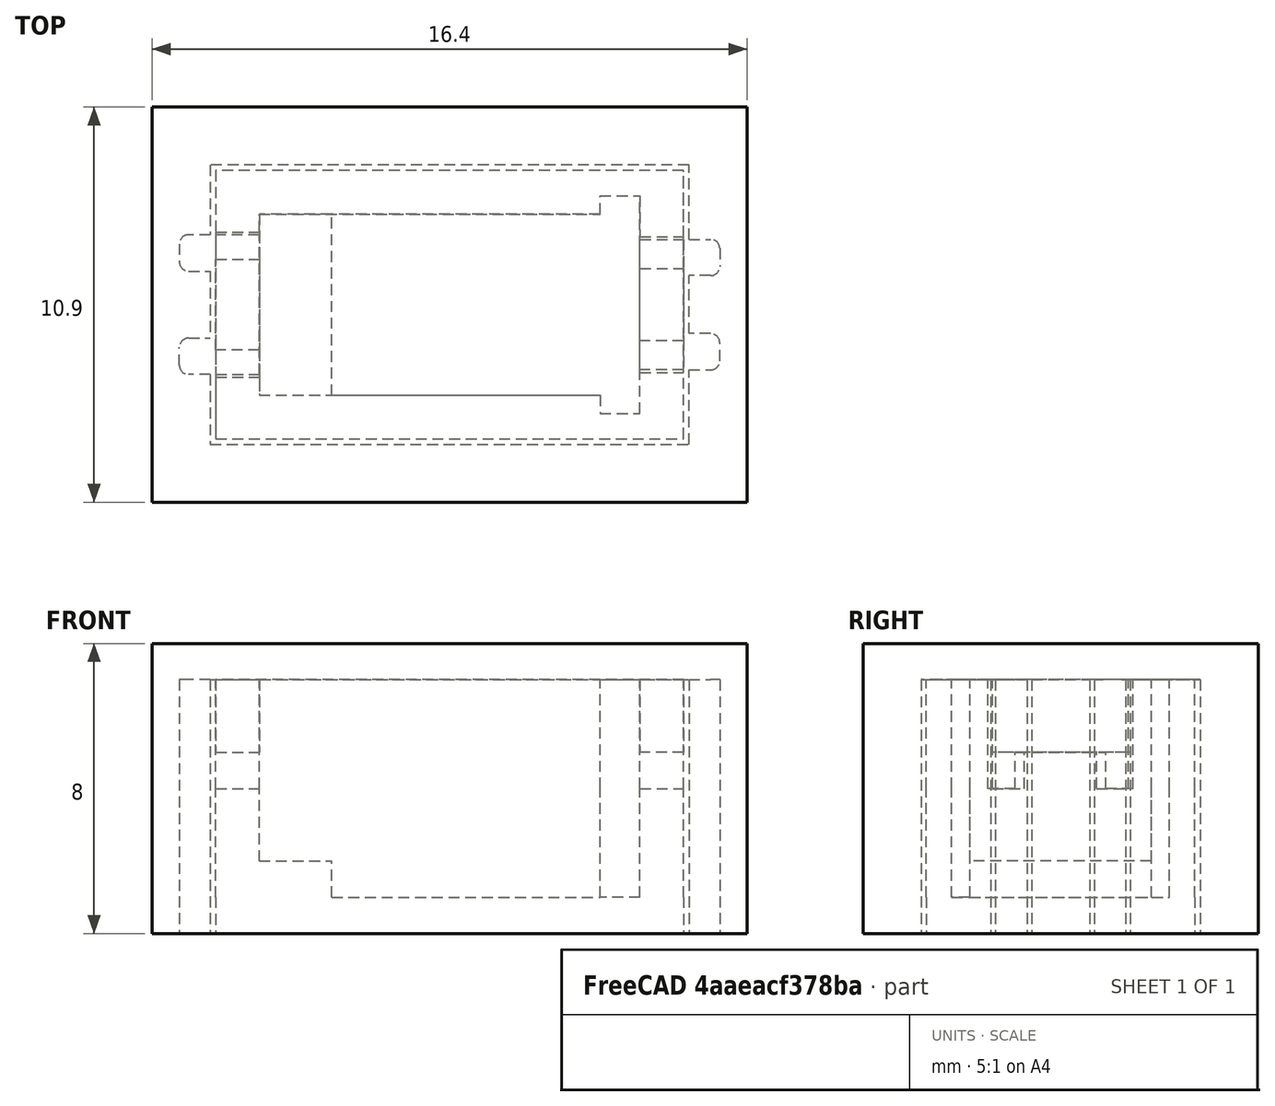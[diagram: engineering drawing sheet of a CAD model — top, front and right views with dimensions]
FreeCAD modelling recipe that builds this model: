
FCSTD DOCUMENT  (FreeCAD 0.19R24415 (Git))
Label: ROCage
License: All rights reserved
LicenseURL: http://en.wikipedia.org/wiki/All_rights_reserved
objects: PartDesign::Pad×8, Sketcher::SketchObject×7, PartDesign::Body×2, Mesh::Feature×2, PartDesign::Pocket×1, PartDesign::ShapeBinder×1, PartDesign::Fillet×1
note: 30 computed .brp shape members not serialized (recipe doc carries the construction recipe); baked Part::Feature solids carry a one-line shape summary decoded from their .brp

FEATURE [Sketcher::SketchObject] Sketch
  FullyConstrained = true
  MapMode = 5
  Support = -> [XY_Plane]
  expr: Constraints[31] = 0.4 * 3
  expr: .Constraints.Wall = 0.4 * 3
  sketch-geometry (12):
    g0: LineSegment StartX=-1.1 StartY=2.5 StartZ=0 EndX=-10.5 EndY=2.5 EndZ=0
    g1: LineSegment StartX=-10.5 StartY=2.5 StartZ=0 EndX=-10.5 EndY=-2.5 EndZ=0
    g2: LineSegment StartX=-10.5 StartY=-2.5 StartZ=0 EndX=-1.1 EndY=-2.5 EndZ=0
    g3: LineSegment StartX=-1.1 StartY=-2.5 StartZ=0 EndX=-1.1 EndY=-3 EndZ=0
    g4: LineSegment StartX=-1.1 StartY=-3 StartZ=0 EndX=0 EndY=-3 EndZ=0
    g5: LineSegment StartX=0 StartY=-3 StartZ=0 EndX=0 EndY=3 EndZ=0
    g6: LineSegment StartX=0 StartY=3 StartZ=0 EndX=-1.1 EndY=3 EndZ=0
    g7: LineSegment StartX=-1.1 StartY=2.5 StartZ=0 EndX=-1.1 EndY=3 EndZ=0
    g8: LineSegment StartX=1.2 StartY=3.7 StartZ=0 EndX=-11.7 EndY=3.7 EndZ=0
    g9: LineSegment StartX=-11.7 StartY=3.7 StartZ=0 EndX=-11.7 EndY=-3.7 EndZ=0
    g10: LineSegment StartX=-11.7 StartY=-3.7 StartZ=0 EndX=1.2 EndY=-3.7 EndZ=0
    g11: LineSegment StartX=1.2 StartY=-3.7 StartZ=0 EndX=1.2 EndY=3.7 EndZ=0
  constraints (34):
    c: Horizontal(g0)
    c: Coincident(g1,g0)
    c: Vertical(g1)
    c: Coincident(g2,g1)
    c: Horizontal(g2)
    c: Coincident(g3,g2)
    c: Vertical(g3)
    c: Coincident(g4,g3)
    c: Vertical(g5)
    c: Coincident(g6,g5)
    c: Horizontal(g6)
    c: Coincident(g7,g0)
    c: Coincident(g7,g6)
    c: Horizontal(g4)
    c: Distance(g1) = 5
    c: DistanceX(g0,g5) = 10.5
    c: Coincident(g4,g5)
    c: Distance(g5) = 6
    c: Distance(g6) = 1.1
    c: Symmetric(g2,g0,g-1)
    c: Symmetric(g6,g3,g-1)
    c: PointOnObject(g-1,g5)
    c: Horizontal(g8)
    c: Coincident(g9,g8)
    c: Coincident(g10,g9)
    c: Horizontal(g10)
    c: Coincident(g11,g10)
    c: Vertical(g11)
    c: Coincident(g11,g8)
    c: Vertical(g9)
    c: DistanceX(g8,g0) = 1.2  'Wall'
    c: DistanceY(g0,g8) = 1.2
    c: DistanceX(g5,g8) = 1.2
    c: DistanceY(g9,g1) = 1.2
FEATURE [PartDesign::Pad] Pad
  Direction = (1,1,1)
  Length = 3
  Length2 = 100
  Profile = -> Sketch
  Type = 0
FEATURE [Sketcher::SketchObject] Sketch001
  ExternalGeometry = -> [Pad]
  FullyConstrained = true
  MapMode = 5
  Placement = pos=(0,0,3) rot=(0,0,1;0rad)
  Support = -> [Pad]
  sketch-geometry (28):
    g0: LineSegment StartX=-11.7 StartY=1.25 StartZ=0 EndX=-10.5 EndY=1.25 EndZ=0
    g1: LineSegment StartX=-10.5 StartY=1.25 StartZ=0 EndX=-10.5 EndY=-1.25 EndZ=0
    g2: LineSegment StartX=-10.5 StartY=-1.25 StartZ=0 EndX=-11.7 EndY=-1.25 EndZ=0
    g3: LineSegment StartX=-11.7 StartY=-1.25 StartZ=0 EndX=-11.7 EndY=1.25 EndZ=0
    g4: LineSegment StartX=0 StartY=1 StartZ=0 EndX=1.2 EndY=1 EndZ=0
    g5: LineSegment StartX=1.2 StartY=1 StartZ=0 EndX=1.2 EndY=-1 EndZ=0
    g6: LineSegment StartX=1.2 StartY=-1 StartZ=0 EndX=0 EndY=-1 EndZ=0
    g7: LineSegment StartX=0 StartY=-1 StartZ=0 EndX=0 EndY=1 EndZ=0
    g8: LineSegment StartX=-11.7 StartY=2 StartZ=0 EndX=-10.5 EndY=2 EndZ=0
    g9: LineSegment StartX=-10.5 StartY=2 StartZ=0 EndX=-10.5 EndY=2.5 EndZ=0
    g10: LineSegment StartX=-10.5 StartY=2.5 StartZ=0 EndX=-1.1 EndY=2.5 EndZ=0
    g11: LineSegment StartX=-1.1 StartY=2.5 StartZ=0 EndX=-1.1 EndY=3 EndZ=0
    g12: LineSegment StartX=-1.1 StartY=3 StartZ=0 EndX=0 EndY=3 EndZ=0
    g13: LineSegment StartX=0 StartY=3 StartZ=0 EndX=0 EndY=1.875 EndZ=0
    g14: LineSegment StartX=0 StartY=1.875 StartZ=0 EndX=1.2 EndY=1.875 EndZ=0
    g15: LineSegment StartX=1.2 StartY=1.875 StartZ=0 EndX=1.2 EndY=3.7 EndZ=0
    g16: LineSegment StartX=1.2 StartY=3.7 StartZ=0 EndX=-11.7 EndY=3.7 EndZ=0
    g17: LineSegment StartX=-11.7 StartY=3.7 StartZ=0 EndX=-11.7 EndY=2 EndZ=0
    g18: LineSegment StartX=-11.7 StartY=-2 StartZ=0 EndX=-10.5 EndY=-2 EndZ=0
    g19: LineSegment StartX=-10.5 StartY=-2 StartZ=0 EndX=-10.5 EndY=-2.5 EndZ=0
    g20: LineSegment StartX=-10.5 StartY=-2.5 StartZ=0 EndX=-1.1 EndY=-2.5 EndZ=0
    g21: LineSegment StartX=-1.1 StartY=-2.5 StartZ=0 EndX=-1.1 EndY=-3 EndZ=0
    g22: LineSegment StartX=-1.1 StartY=-3 StartZ=0 EndX=0 EndY=-3 EndZ=0
    g23: LineSegment StartX=0 StartY=-3 StartZ=0 EndX=0 EndY=-1.875 EndZ=0
    g24: LineSegment StartX=0 StartY=-1.875 StartZ=0 EndX=1.2 EndY=-1.875 EndZ=0
    g25: LineSegment StartX=1.2 StartY=-1.875 StartZ=0 EndX=1.2 EndY=-3.7 EndZ=0
    g26: LineSegment StartX=1.2 StartY=-3.7 StartZ=0 EndX=-11.7 EndY=-3.7 EndZ=0
    g27: LineSegment StartX=-11.7 StartY=-3.7 StartZ=0 EndX=-11.7 EndY=-2 EndZ=0
  constraints (68):
    c: Coincident(g0,g1)
    c: Coincident(g1,g2)
    c: Coincident(g2,g3)
    c: Coincident(g3,g0)
    c: Horizontal(g0)
    c: Horizontal(g2)
    c: Vertical(g3)
    c: Coincident(g4,g5)
    c: Coincident(g5,g6)
    c: Coincident(g6,g7)
    c: Coincident(g7,g4)
    c: Horizontal(g4)
    c: Horizontal(g6)
    c: Vertical(g5)
    c: PointOnObject(g0,g-3)
    c: PointOnObject(g0,g-4)
    c: PointOnObject(g4,g-11)
    c: PointOnObject(g4,g-14)
    c: Symmetric(g1,g0,g-1)
    c: Symmetric(g4,g6,g-1)
    c: PointOnObject(g8,g-3)
    c: PointOnObject(g8,g-4)
    c: Horizontal(g8)
    c: Coincident(g9,g8)
    c: Coincident(g9,g-5)
    c: Coincident(g10,g9)
    c: Coincident(g10,g-12)
    c: Coincident(g11,g10)
    c: Coincident(g11,g-13)
    c: Coincident(g12,g11)
    c: Coincident(g12,g-13)
    c: Coincident(g13,g12)
    c: PointOnObject(g13,g-11)
    c: Coincident(g14,g13)
    c: PointOnObject(g14,g-14)
    c: Horizontal(g14)
    c: Coincident(g15,g14)
    c: Coincident(g15,g-14)
    c: Coincident(g16,g15)
    c: Coincident(g16,g-6)
    c: Coincident(g17,g16)
    c: Coincident(g17,g8)
    c: PointOnObject(g18,g-3)
    c: Coincident(g19,g18)
    c: Coincident(g19,g-8)
    c: Coincident(g20,g19)
    c: Coincident(g20,g-9)
    c: Coincident(g21,g-10)
    c: Coincident(g22,g21)
    c: Coincident(g22,g-11)
    c: PointOnObject(g24,g-14)
    c: Coincident(g25,g24)
    c: Coincident(g25,g-14)
    c: Coincident(g26,g25)
    c: Coincident(g26,g-7)
    c: Coincident(g27,g26)
    c: Coincident(g27,g18)
    c: Distance(g3) = 2.5
    c: Symmetric(g8,g18,g-1)
    c: Distance(g18,g8) = 4
    c: Horizontal(g18)
    c: Distance(g5) = 2
    c: Distance(g24,g14) = 3.75
    c: Horizontal(g24)
    c: Coincident(g23,g24)
    c: Symmetric(g23,g13,g-1)
    c: Coincident(g21,g20)
    c: Coincident(g23,g22)
FEATURE [PartDesign::Pad] Pad001
  BaseFeature = -> Pad
  Direction = (1,1,1)
  Length = 3
  Length2 = 100
  Profile = -> Sketch001
  Type = 0
FEATURE [PartDesign::Pad] Pad002
  BaseFeature = -> Pad001
  Direction = (1,1,1)
  Length = 0.0001
  Length2 = 100
  Profile = -> Pad001 [Face10,Face8]
  Type = 0
FEATURE [PartDesign::Pocket] Pocket
  BaseFeature = -> Pad002
  Length = 2
  Length2 = 100
  Profile = -> Pad002 [Face38,Face32]
  Type = 0
FEATURE [Sketcher::SketchObject] Sketch002
  ExternalGeometry = -> [Pocket]
  FullyConstrained = true
  MapMode = 5
  Placement = pos=(0,0,0) rot=(1,0,0;3.14159rad)
  Support = -> [Pocket]
  sketch-geometry (4):
    g0: LineSegment StartX=-11.7 StartY=3.7 StartZ=0 EndX=1.2 EndY=3.7 EndZ=0
    g1: LineSegment StartX=1.2 StartY=3.7 StartZ=0 EndX=1.2 EndY=-3.7 EndZ=0
    g2: LineSegment StartX=1.2 StartY=-3.7 StartZ=0 EndX=-11.7 EndY=-3.7 EndZ=0
    g3: LineSegment StartX=-11.7 StartY=-3.7 StartZ=0 EndX=-11.7 EndY=3.7 EndZ=0
  constraints (10):
    c: Coincident(g0,g1)
    c: Coincident(g1,g2)
    c: Coincident(g2,g3)
    c: Coincident(g3,g0)
    c: Horizontal(g0)
    c: Horizontal(g2)
    c: Vertical(g1)
    c: Vertical(g3)
    c: Coincident(g0,g-3)
    c: Coincident(g1,g-4)
FEATURE [PartDesign::Pad] Pad003
  BaseFeature = -> Pocket
  Direction = (1,1,1)
  Length = 1
  Length2 = 100
  Profile = -> Sketch002
  Type = 0
FEATURE [Sketcher::SketchObject] Sketch003
  ExternalGeometry = -> [Pad003]
  FullyConstrained = true
  MapMode = 5
  Support = -> [Pad003]
  sketch-geometry (4):
    g0: LineSegment StartX=-10.5 StartY=-2.5 StartZ=0 EndX=-8.5 EndY=-2.5 EndZ=0
    g1: LineSegment StartX=-8.5 StartY=-2.5 StartZ=0 EndX=-8.5 EndY=2.5 EndZ=0
    g2: LineSegment StartX=-8.5 StartY=2.5 StartZ=0 EndX=-10.5 EndY=2.5 EndZ=0
    g3: LineSegment StartX=-10.5 StartY=2.5 StartZ=0 EndX=-10.5 EndY=-2.5 EndZ=0
  constraints (10):
    c: Coincident(g0,g1)
    c: Coincident(g1,g2)
    c: Coincident(g2,g3)
    c: Coincident(g3,g0)
    c: Horizontal(g0)
    c: Horizontal(g2)
    c: Vertical(g1)
    c: Coincident(g0,g-4)
    c: Coincident(g2,g-3)
    c: Distance(g2) = 2
FEATURE [PartDesign::Pad] Pad004
  BaseFeature = -> Pad003
  Direction = (1,1,1)
  Length = 1
  Length2 = 100
  Profile = -> Sketch003
  Type = 0
FEATURE [PartDesign::Body] Body  label="ROCageHolder"
  Group = -> [Sketch,Pad,Sketch001,Pad001,Pad002,Pocket,Sketch002,Pad003,Sketch003,Pad004]
  Origin = -> Origin
  Tip = -> Pad004
FEATURE [PartDesign::ShapeBinder] ReferencePad004
  Placement = pos=(0,0,3) rot=(0,0,1;0rad)
  Support = -> [Pad004]
  TraceSupport = false
FEATURE [Sketcher::SketchObject] Sketch004
  ExternalGeometry = -> [ReferencePad004]
  FullyConstrained = true
  MapMode = 5
  Placement = pos=(0,0,6) rot=(0,0,1;0rad)
  Support = -> [ReferencePad004]
  expr: Constraints[7] = 0.4 * 4 + 0.15
  sketch-geometry (4):
    g0: LineSegment StartX=-13.45 StartY=5.45 StartZ=0 EndX=2.95 EndY=5.45 EndZ=0
    g1: LineSegment StartX=2.95 StartY=5.45 StartZ=0 EndX=2.95 EndY=-5.45 EndZ=0
    g2: LineSegment StartX=2.95 StartY=-5.45 StartZ=0 EndX=-13.45 EndY=-5.45 EndZ=0
    g3: LineSegment StartX=-13.45 StartY=-5.45 StartZ=0 EndX=-13.45 EndY=5.45 EndZ=0
  constraints (11):
    c: Coincident(g0,g1)
    c: Coincident(g1,g2)
    c: Coincident(g2,g3)
    c: Coincident(g3,g0)
    c: Horizontal(g0)
    c: Horizontal(g2)
    c: Vertical(g1)
    c: DistanceX(g0,g-3) = 1.75
    c: DistanceY(g-3,g0) = 1.75
    c: DistanceX(g-4,g0) = 1.75
    c: Symmetric(g2,g0,g-1)
FEATURE [PartDesign::Pad] Pad005
  Direction = (1,1,1)
  Length = 1
  Length2 = 100
  Placement = pos=(0,0,3) rot=(0,0,1;0rad)
  Profile = -> Sketch004
  Type = 0
FEATURE [Sketcher::SketchObject] Sketch005
  ExternalGeometry = -> [Pad005]
  FullyConstrained = true
  MapMode = 5
  Placement = pos=(0,0,6) rot=(1,0,0;3.14159rad)
  Support = -> [Pad005]
  sketch-geometry (8):
    g0: LineSegment StartX=-11.7 StartY=1.925 StartZ=0 EndX=-10.5 EndY=1.925 EndZ=0
    g1: LineSegment StartX=-10.5 StartY=1.925 StartZ=0 EndX=-10.5 EndY=-1.925 EndZ=0
    g2: LineSegment StartX=-10.5 StartY=-1.925 StartZ=0 EndX=-11.7 EndY=-1.925 EndZ=0
    g3: LineSegment StartX=-11.7 StartY=-1.925 StartZ=0 EndX=-11.7 EndY=1.925 EndZ=0
    g4: LineSegment StartX=1.2 StartY=1.8 StartZ=0 EndX=-7e-16 EndY=1.8 EndZ=0
    g5: LineSegment StartX=-7e-16 StartY=1.8 StartZ=0 EndX=-7e-16 EndY=-1.8 EndZ=0
    g6: LineSegment StartX=-7e-16 StartY=-1.8 StartZ=0 EndX=1.2 EndY=-1.8 EndZ=0
    g7: LineSegment StartX=1.2 StartY=-1.8 StartZ=0 EndX=1.2 EndY=1.8 EndZ=0
  constraints (22):
    c: Coincident(g0,g1)
    c: Coincident(g1,g2)
    c: Coincident(g2,g3)
    c: Coincident(g3,g0)
    c: Horizontal(g0)
    c: Horizontal(g2)
    c: Vertical(g1)
    c: Coincident(g4,g5)
    c: Coincident(g5,g6)
    c: Coincident(g6,g7)
    c: Coincident(g7,g4)
    c: Horizontal(g4)
    c: Horizontal(g6)
    c: Vertical(g5)
    c: DistanceX(g-3,g0) = 1.75
    c: DistanceX(g0,g0) = 1.2
    c: Distance(g1) = 3.85
    c: DistanceX(g4,g-4) = 1.75
    c: DistanceX(g4,g4) = 1.2
    c: Symmetric(g6,g4,g-1)
    c: Symmetric(g0,g2,g-1)
    c: Distance(g5) = 3.6
FEATURE [PartDesign::Pad] Pad006
  BaseFeature = -> Pad005
  Direction = (1,1,1)
  Length = 2
  Length2 = 100
  Placement = pos=(0,0,3) rot=(0,0,1;0rad)
  Profile = -> Sketch005
  Type = 0
FEATURE [Sketcher::SketchObject] Sketch006
  ExternalGeometry = -> [Pad006]
  FullyConstrained = true
  MapMode = 5
  Placement = pos=(0,0,6) rot=(1,0,0;3.14159rad)
  Support = -> [Pad006]
  sketch-geometry (24):
    g0: LineSegment StartX=-13.45 StartY=5.45 StartZ=0 EndX=2.95 EndY=5.45 EndZ=0
    g1: LineSegment StartX=2.95 StartY=5.45 StartZ=0 EndX=2.95 EndY=-5.45 EndZ=0
    g2: LineSegment StartX=2.95 StartY=-5.45 StartZ=0 EndX=-13.45 EndY=-5.45 EndZ=0
    g3: LineSegment StartX=-13.45 StartY=-5.45 StartZ=0 EndX=-13.45 EndY=5.45 EndZ=0
    g4: LineSegment StartX=-11.85 StartY=3.85 StartZ=0 EndX=1.35 EndY=3.85 EndZ=0
    g5: LineSegment StartX=1.35 StartY=3.85 StartZ=0 EndX=1.35 EndY=1.8 EndZ=0
    g6: LineSegment StartX=1.35 StartY=-3.85 StartZ=0 EndX=-11.85 EndY=-3.85 EndZ=0
    g7: LineSegment StartX=-11.85 StartY=-3.85 StartZ=0 EndX=-11.85 EndY=-1.925 EndZ=0
    g8: LineSegment StartX=-11.85 StartY=1.925 StartZ=0 EndX=-12.7 EndY=1.925 EndZ=0
    g9: LineSegment StartX=-12.7 StartY=1.925 StartZ=0 EndX=-12.7 EndY=0.925 EndZ=0
    g10: LineSegment StartX=-12.7 StartY=0.925 StartZ=0 EndX=-11.85 EndY=0.925 EndZ=0
    g11: LineSegment StartX=-11.85 StartY=-1.925 StartZ=0 EndX=-12.7 EndY=-1.925 EndZ=0
    g12: LineSegment StartX=-12.7 StartY=-1.925 StartZ=0 EndX=-12.7 EndY=-0.925 EndZ=0
    g13: LineSegment StartX=-12.7 StartY=-0.925 StartZ=0 EndX=-11.85 EndY=-0.925 EndZ=0
    g14: LineSegment StartX=1.35 StartY=1.8 StartZ=0 EndX=2.2 EndY=1.8 EndZ=0
    g15: LineSegment StartX=1.35 StartY=-1.8 StartZ=0 EndX=2.2 EndY=-1.8 EndZ=0
    g16: LineSegment StartX=2.2 StartY=-1.8 StartZ=0 EndX=2.2 EndY=-0.8 EndZ=0
    g17: LineSegment StartX=2.2 StartY=-0.8 StartZ=0 EndX=1.35 EndY=-0.8 EndZ=0
    g18: LineSegment StartX=2.2 StartY=1.8 StartZ=0 EndX=2.2 EndY=0.8 EndZ=0
    g19: LineSegment StartX=2.2 StartY=0.8 StartZ=0 EndX=1.35 EndY=0.8 EndZ=0
    g20: LineSegment StartX=-11.85 StartY=1.925 StartZ=0 EndX=-11.85 EndY=3.85 EndZ=0
    g21: LineSegment StartX=-11.85 StartY=-0.925 StartZ=0 EndX=-11.85 EndY=0.925 EndZ=0
    g22: LineSegment StartX=1.35 StartY=0.8 StartZ=0 EndX=1.35 EndY=-0.8 EndZ=0
    g23: LineSegment StartX=1.35 StartY=-1.8 StartZ=0 EndX=1.35 EndY=-3.85 EndZ=0
  constraints (65):
    c: Coincident(g0,g1)
    c: Coincident(g1,g2)
    c: Coincident(g2,g3)
    c: Coincident(g3,g0)
    c: Horizontal(g0)
    c: Horizontal(g2)
    c: Vertical(g1)
    c: Vertical(g3)
    c: Coincident(g0,g-3)
    c: Coincident(g1,g-4)
    c: Coincident(g4,g5)
    c: Coincident(g23,g6)
    c: Coincident(g6,g7)
    c: Coincident(g20,g4)
    c: Horizontal(g4)
    c: Horizontal(g6)
    c: Vertical(g7)
    c: DistanceX(g0,g4) = 1.6
    c: DistanceX(g4,g0) = 1.6
    c: DistanceY(g4,g0) = 1.6
    c: Symmetric(g4,g23,g-1)
    c: Coincident(g9,g8)
    c: Vertical(g9)
    c: Coincident(g10,g9)
    c: Horizontal(g11)
    c: Coincident(g12,g11)
    c: Coincident(g13,g12)
    c: Horizontal(g13)
    c: Horizontal(g8)
    c: Vertical(g12)
    c: Vertical(g9,g12)
    c: Distance(g9) = 1
    c: Distance(g12) = 1
    c: Horizontal(g10)
    c: Horizontal(g14)
    c: Horizontal(g15)
    c: Coincident(g16,g15)
    c: Vertical(g16)
    c: Coincident(g17,g16)
    c: Horizontal(g17)
    c: Coincident(g18,g14)
    c: Vertical(g18)
    c: Coincident(g19,g18)
    c: Horizontal(g19)
    c: Distance(g18) = 1
    c: Distance(g16) = 1
    c: Vertical(g16,g18)
    c: Tangent(g7,g20)
    c: Coincident(g8,g20)
    c: Coincident(g10,g21)
    c: Distance(g-5,g8) = 1
    c: Horizontal(g-5,g8)
    c: Tangent(g7,g21)
    c: Coincident(g13,g21)
    c: Coincident(g11,g7)
    c: Horizontal(g-6,g7)
    c: Tangent(g5,g22)
    c: Tangent(g22,g23)
    c: Coincident(g14,g5)
    c: Coincident(g19,g22)
    c: Coincident(g17,g22)
    c: Coincident(g15,g23)
    c: Horizontal(g-8,g5)
    c: Horizontal(g-7,g15)
    c: Distance(g-8,g14) = 1
FEATURE [PartDesign::Pad] Pad007
  BaseFeature = -> Pad006
  Direction = (1,1,1)
  Length = 7
  Length2 = 100
  Placement = pos=(0,0,3) rot=(0,0,1;0rad)
  Profile = -> Sketch006
  Type = 0
FEATURE [PartDesign::Fillet] Fillet
  Base = -> Pad007 [Edge72,Edge64,Edge70,Edge62,Edge52,Edge44,Edge50,Edge42]
  BaseFeature = -> Pad007
  Placement = pos=(0,0,3) rot=(0,0,1;0rad)
  Radius = 0.25
  SupportTransform = false
FEATURE [PartDesign::Body] Body001  label="ROCageLid"
  Group = -> [ReferencePad004,Sketch004,Pad005,Sketch005,Pad006,Sketch006,Pad007,Fillet]
  Origin = -> Origin001
  Tip = -> Fillet
FEATURE [Mesh::Feature] Mesh  label="ROCageHolder (Meshed)"
FEATURE [Mesh::Feature] Mesh001  label="ROCageLid (Meshed)"
